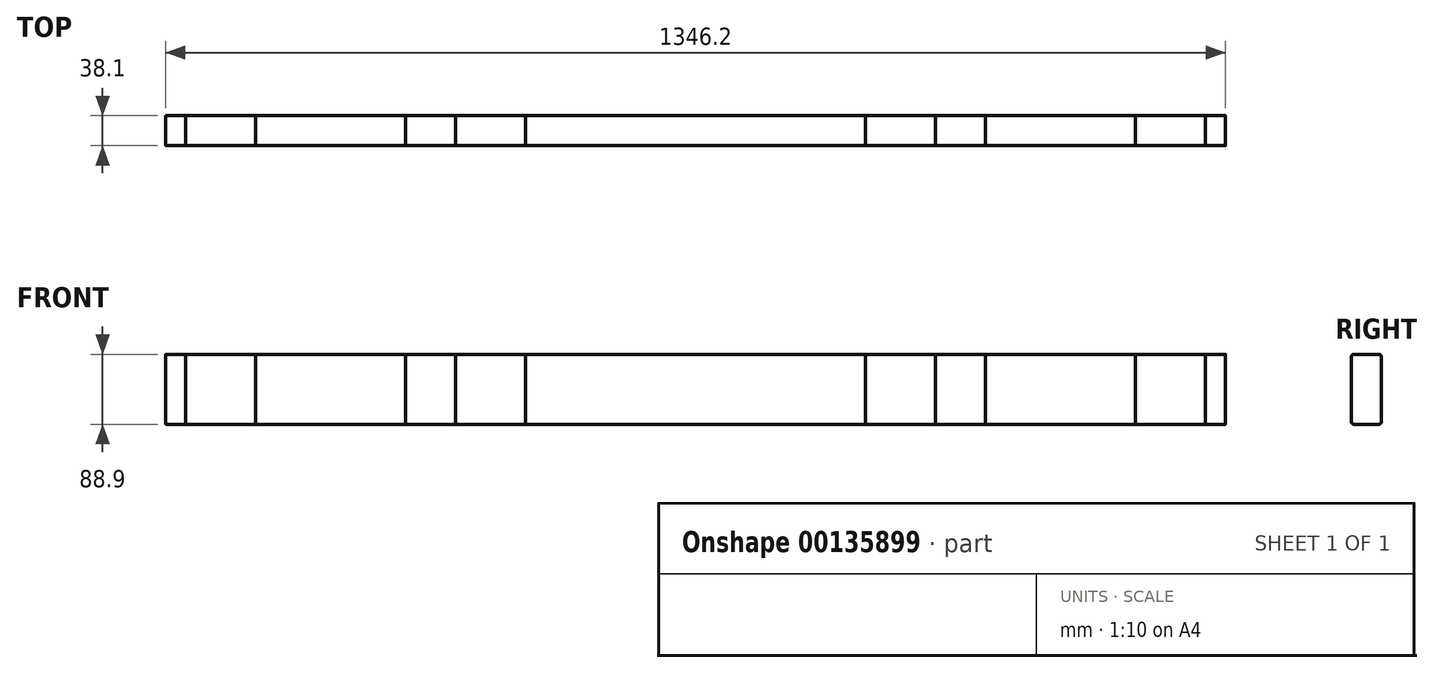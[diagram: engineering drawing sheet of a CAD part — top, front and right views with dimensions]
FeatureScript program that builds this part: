
annotation { "Feature Type Name" : "Feature", "Feature Type Description" : "" }
export const myFeature = defineFeature(function(context is Context, id is Id, definition is map)
    precondition{}
    {
        {
            var Q0;
            Q0=qCreatedBy(makeId("Right.planeOp"),FACE);
            var sketch = newSketch(context, id + "F0", { "sketchPlane" : qUnion([Q0])});
            skLineSegment(sketch, "E0.bottom", {"start": v(15.87, 44.45) * mm, "end": v(-15.88, 44.45) * mm});
            skLineSegment(sketch, "E0.top", {"start": v(15.87, -44.45) * mm, "end": v(-15.88, -44.45) * mm});
            skLineSegment(sketch, "E0.left", {"start": v(19.05, 41.28) * mm, "end": v(19.05, -41.27) * mm});
            skLineSegment(sketch, "E0.right", {"start": v(-19.05, 41.28) * mm, "end": v(-19.05, -41.27) * mm});
            skPoint(sketch, "E0.middle", {"position": v(0, 0) * mm});
            skPoint(sketch, "E1.visualSharp", {"position": v(19.05, 44.45) * mm});
            skArc(sketch, "E1.filletArc", {"start": v(19.05, 41.28) * mm, "mid": v(18.12, 43.52) * mm, "end": v(15.87, 44.45) * mm});
            skPoint(sketch, "E2.visualSharp", {"position": v(19.05, -44.45) * mm});
            skArc(sketch, "E2.filletArc", {"start": v(15.87, -44.45) * mm, "mid": v(18.12, -43.52) * mm, "end": v(19.05, -41.27) * mm});
            skPoint(sketch, "E3.visualSharp", {"position": v(-19.05, -44.45) * mm});
            skArc(sketch, "E3.filletArc", {"start": v(-19.05, -41.27) * mm, "mid": v(-18.12, -43.52) * mm, "end": v(-15.88, -44.45) * mm});
            skPoint(sketch, "E4.visualSharp", {"position": v(-19.05, 44.45) * mm});
            skArc(sketch, "E4.filletArc", {"start": v(-15.88, 44.45) * mm, "mid": v(-18.12, 43.52) * mm, "end": v(-19.05, 41.28) * mm});
            skSolve(sketch);
        }
        {
            var Q0;
            Q0=makeQuery(id+"F0.imprint","IMPRINT",FACE,{"disambiguationData":[TD([[makeQuery(id+"F0.imprint","IMPRINT",EDGE,{"derivedFrom":sQuery(id+"F0.wireOp",EDGE,"E0.bottom")}),1.0]])]});
            extrude(context, id + "F1", {"entities" : qUnion([Q0]), "endBound" : BoundingType.SYMMETRIC, "depth" : 736.6 * mm});
        }
        {
            var Q0;
            Q0=makeQuery(id+"F0.imprint","IMPRINT",FACE,{"disambiguationData":[TD([[makeQuery(id+"F0.imprint","IMPRINT",EDGE,{"derivedFrom":sQuery(id+"F0.wireOp",EDGE,"E0.bottom")}),1.0]])]});
            extrude(context, id + "F2", {"entities" : qUnion([Q0]), "endBound" : BoundingType.SYMMETRIC, "depth" : 431.8 * mm});
        }
        {
            var Q0;
            Q0=makeQuery(id+"F0.imprint","IMPRINT",FACE,{"disambiguationData":[TD([[makeQuery(id+"F0.imprint","IMPRINT",EDGE,{"derivedFrom":sQuery(id+"F0.wireOp",EDGE,"E0.bottom")}),1.0]])]});
            extrude(context, id + "F3", {"entities" : qUnion([Q0]), "endBound" : BoundingType.SYMMETRIC, "depth" : 609.6 * mm});
        }
        {
            var Q0;
            Q0 = qSketchRegion(id + "F0", true);
            extrude(context, id + "F4", {"entities" : qUnion([Q0]), "endBound" : BoundingType.SYMMETRIC, "depth" : 1117.6 * mm});
        }
        {
            var Q0;
            Q0 = qSketchRegion(id + "F0", true);
            extrude(context, id + "F5", {"entities" : qUnion([Q0]), "endBound" : BoundingType.SYMMETRIC, "depth" : 1295.4 * mm});
        }
        {
            var Q0;
            Q0=makeQuery(id+"F0.imprint","IMPRINT",FACE,{"disambiguationData":[TD([[makeQuery(id+"F0.imprint","IMPRINT",EDGE,{"derivedFrom":sQuery(id+"F0.wireOp",EDGE,"E0.bottom")}),1.0]])]});
            extrude(context, id + "F6", {"entities" : qUnion([Q0]), "endBound" : BoundingType.SYMMETRIC, "depth" : 1346.2 * mm});
        }
    });
